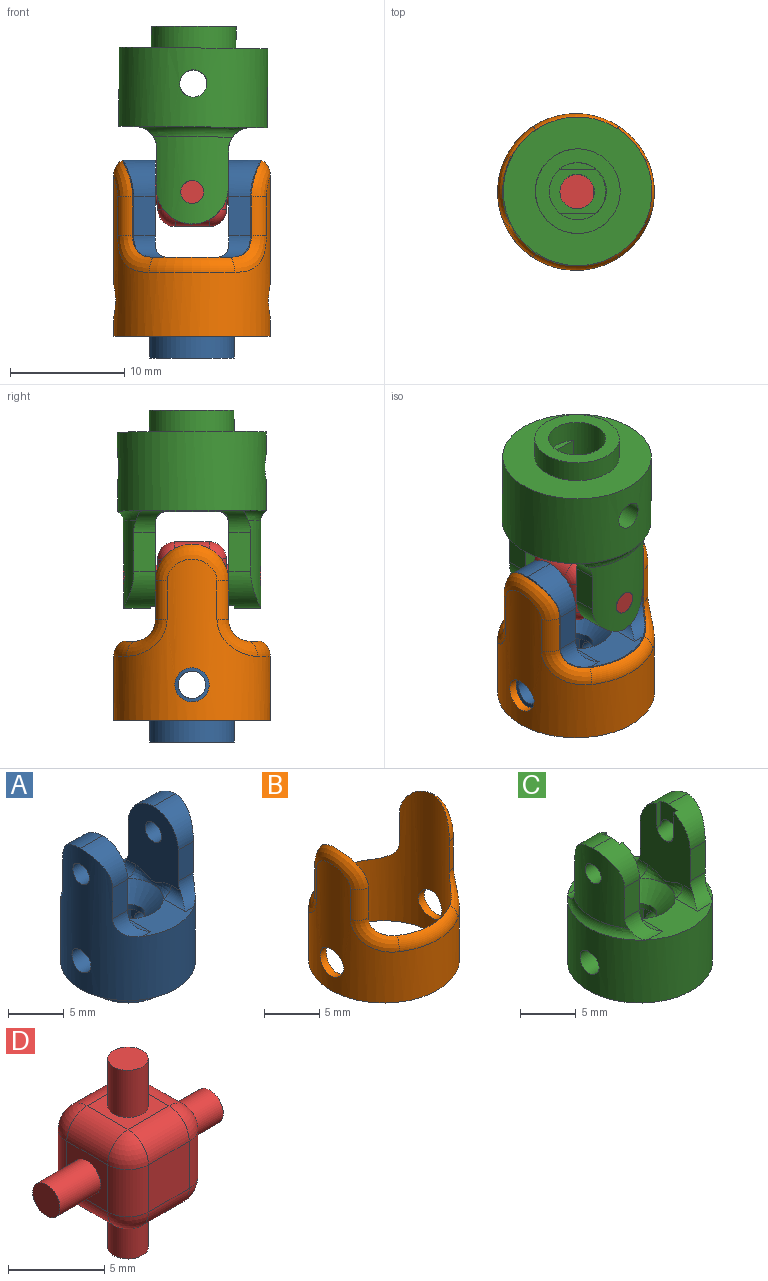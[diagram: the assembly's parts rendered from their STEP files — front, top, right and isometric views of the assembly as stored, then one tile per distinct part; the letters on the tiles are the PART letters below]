
ASSEMBLY  parts=4 mates=3
PART A: 38 faces, bbox 12x12x17.3 mm
  f0: plane 6.48x3.75mm, normal (0,0,1), area 13.8mm2, adj f8,f27,f28,f30,f32,f35
  f1: plane 6.48x3.75mm, normal (0,0,1), area 13.8mm2, adj f8,f27,f29,f31,f34,f37
  f2: cylinder r=2.5mm len=6.6mm, axis (0,0,-1), area 71.9mm2, adj f4,f5,f7,f9,f10,f12
  f3: cylinder r=3.7mm len=7.4mm, axis (0,0,-1), area 44.2mm2, adj f4,f6
  f4: plane 7.4x7.4mm, normal (0,0,-1), area 23.4mm2, adj f2,f3
  f5: plane 3.13x0.55mm, normal (0,0,-1), area 1.2mm2, adj f2,f9
  f6: plane 12x12mm, normal (0,0,-1), area 70.1mm2, adj f3,f8
  f7: plane 4.7x3.13mm, normal (-1,0,0), area 10.2mm2, adj f2,f10,f12,f22
  f8: cylinder r=6mm len=15.4mm, axis (0,0,-1), area 351mm2, adj f0,f1,f6,f13,f14,f16,f18,f19
  f9: plane 4.7x3.13mm, normal (1,0,0), area 10.2mm2, adj f2,f5,f12,f21
  f10: plane 3.13x0.55mm, normal (0,0,-1), area 1.2mm2, adj f2,f7
  f11: cylinder r=1.5mm len=3mm, axis (0,0,-1), area 5.2mm2, adj f12,f27
  f12: plane 5x3.9mm, normal (0,0,-1), area 10.2mm2, adj f2,f7,f9,f11
  f13: plane 3.4x1.91mm, normal (0,1,0), area 6.5mm2, adj f8,f15,f25,f31
  f14: plane 3.4x1.91mm, normal (0,-1,0), area 6.5mm2, adj f8,f15,f26,f30
  f15: plane 8.19x6.75mm, normal (1,0,0), area 40.9mm2, adj f13,f14,f20,f25,f26,f30,f31,f35
  f16: plane 3.4x1.91mm, normal (0,1,0), area 6.5mm2, adj f8,f17,f23,f29
  f17: plane 8.19x6.75mm, normal (-1,0,0), area 40.9mm2, adj f16,f18,f19,f23,f24,f28,f29,f32
  f18: plane 3.4x1.91mm, normal (0,-1,0), area 6.5mm2, adj f8,f17,f24,f28
  f19: cylinder r=1.05mm len=2.8mm, axis (1,0,0), area 18.5mm2, adj f8,f17
  f20: cylinder r=1.05mm len=2.8mm, axis (1,0,0), area 18.5mm2, adj f8,f15
  f21: cylinder r=1.2mm len=4.05mm, axis (1,0,0), area 30.5mm2, adj f8,f9
  f22: cylinder r=1.2mm len=4.05mm, axis (1,0,0), area 30.5mm2, adj f7,f8
  f23: cylinder r=3.2mm len=3.2mm, axis (1,0,0), area 11.7mm2, adj f8,f16,f17,f24
  f24: cylinder r=3.2mm len=3.2mm, axis (-1,0,0), area 11.7mm2, adj f8,f17,f18,f23
  f25: cylinder r=3.2mm len=3.2mm, axis (1,0,0), area 11.7mm2, adj f8,f13,f15,f26
  f26: cylinder r=3.2mm len=3.2mm, axis (-1,0,0), area 11.7mm2, adj f8,f14,f15,f25
  f27: cone r=1.5mm half-angle=45deg, axis (0,0,1), area 34.1mm2, adj f0,f1,f11,f33,f36
  f28: cylinder r=1.9mm len=2.91mm, axis (1,0,0), area 5mm2, adj f0,f8,f17,f18,f32
  f29: cylinder r=1.9mm len=2.91mm, axis (-1,0,0), area 5mm2, adj f1,f8,f16,f17,f34
  f30: cylinder r=1.9mm len=2.91mm, axis (1,0,0), area 5mm2, adj f0,f8,f14,f15,f35
  f31: cylinder r=1.9mm len=2.91mm, axis (-1,0,0), area 5mm2, adj f1,f8,f13,f15,f37
  f32: cylinder r=1mm len=2.8mm, axis (0,-1,0), area 3.1mm2, adj f0,f17,f28,f33
  f33: bspline ~4.87x1.14mm, area 3.8mm2, adj f17,f27,f32,f34
  f34: cylinder r=1mm len=2.8mm, axis (0,-1,0), area 3.1mm2, adj f1,f17,f29,f33
  f35: cylinder r=1mm len=2.8mm, axis (0,1,0), area 3.1mm2, adj f0,f15,f30,f36
  f36: bspline ~4.87x1.14mm, area 3.8mm2, adj f15,f27,f35,f37
  f37: cylinder r=1mm len=2.8mm, axis (0,1,0), area 3.1mm2, adj f1,f15,f31,f36
PART B: 17 faces, bbox 13.7x14.8x15.4 mm
  f0: cylinder r=6.1mm len=15.4mm, axis (0,0,-1), area 358.9mm2, adj f2,f3,f4,f5,f6,f7,f8,f9
  f1: cylinder r=6.85mm len=14.1mm, axis (0,0,-1), area 310mm2, adj f2,f3,f4,f5,f6,f7,f8,f9
  f2: plane 13.7x13.7mm, normal (0,0,-1), area 30.5mm2, adj f0,f1
  f3: cylinder r=1.5mm len=3mm, axis (-1,0,0), area 7.1mm2, adj f0,f1
  f4: cylinder r=1.5mm len=3mm, axis (-1,0,0), area 7.1mm2, adj f0,f1
  f5: bspline ~6.4x3.2mm, area 14.3mm2, adj f0,f1,f6,f7
  f6: cylinder r=1.5mm len=3.4mm, axis (0,0,1), area 5.9mm2, adj f0,f1,f5,f8
  f7: cylinder r=1.5mm len=3.4mm, axis (0,0,1), area 5.9mm2, adj f0,f1,f5,f9
  f8: bspline ~3.54x3.2mm, area 8mm2, adj f0,f1,f6,f10
  f9: bspline ~3.54x3.2mm, area 8mm2, adj f0,f1,f7,f11
  f10: torus R=5.35mm, axis (0,0,1), area 12mm2, adj f0,f1,f8,f12
  f11: torus R=5.35mm, axis (0,0,1), area 12mm2, adj f0,f1,f9,f13
  f12: bspline ~3.54x3.2mm, area 8mm2, adj f0,f1,f10,f14
  f13: bspline ~3.54x3.2mm, area 8mm2, adj f0,f1,f11,f15
  f14: cylinder r=1.5mm len=3.4mm, axis (0,0,1), area 5.9mm2, adj f0,f1,f12,f16
  f15: cylinder r=1.5mm len=3.4mm, axis (0,0,1), area 5.9mm2, adj f0,f1,f13,f16
  f16: bspline ~6.4x3.81mm, area 14.3mm2, adj f0,f1,f14,f15
PART C: 52 faces, bbox 15.2x13x17.3 mm
  f0: plane 8.18x4.25mm, normal (0,0,1), area 17.7mm2, adj f12,f39,f41,f42,f44,f49
  f1: plane 7.99x6.75mm, normal (1,0,0), area 37mm2, adj f4,f17,f19,f25,f26,f28,f29,f37
  f2: plane 7.99x6.75mm, normal (-1,0,0), area 37mm2, adj f3,f21,f22,f30,f31,f33,f34,f35
  f3: cylinder r=1mm len=2.8mm, axis (1,0,0), area 16.2mm2, adj f2,f20,f32,f33,f34
  f4: cylinder r=1mm len=2.8mm, axis (1,0,0), area 16.2mm2, adj f1,f18,f25,f26,f27
  f5: plane 8.18x4.25mm, normal (0,0,1), area 17.7mm2, adj f12,f39,f40,f43,f46,f51
  f6: cylinder r=2.5mm len=6.6mm, axis (0,0,-1), area 71.9mm2, adj f8,f9,f11,f13,f14,f16
  f7: cylinder r=3.7mm len=7.4mm, axis (0,0,-1), area 44.2mm2, adj f8,f10
  f8: plane 7.4x7.4mm, normal (0,0,-1), area 23.4mm2, adj f6,f7
  f9: plane 3.13x0.55mm, normal (0,0,-1), area 1.2mm2, adj f6,f13
  f10: plane 13x13mm, normal (0,0,-1), area 89.7mm2, adj f7,f12
  f11: plane 4.7x3.13mm, normal (-1,0,0), area 10.2mm2, adj f6,f14,f16,f24
  f12: cylinder r=6.5mm len=13mm, axis (0,0,-1), area 272.7mm2, adj f0,f5,f10,f23,f24,f47,f48
  f13: plane 4.7x3.13mm, normal (1,0,0), area 10.2mm2, adj f6,f9,f16,f23
  f14: plane 3.13x0.55mm, normal (0,0,-1), area 1.2mm2, adj f6,f11
  f15: cylinder r=1.5mm len=3mm, axis (0,0,-1), area 5.2mm2, adj f16,f39
  f16: plane 5x3.9mm, normal (0,0,-1), area 10.2mm2, adj f6,f11,f13,f15
  f17: plane 3.4x1.91mm, normal (0,1,0), area 6.5mm2, adj f1,f18,f37,f43
  f18: cylinder r=6mm len=7.63mm, axis (0,0,-1), area 43mm2, adj f4,f17,f19,f37,f38,f42,f43,f48
  f19: plane 3.4x1.91mm, normal (0,-1,0), area 6.5mm2, adj f1,f18,f38,f42
  f20: cylinder r=6mm len=7.63mm, axis (0,0,-1), area 43mm2, adj f3,f21,f22,f35,f36,f40,f41,f47
  f21: plane 3.4x1.91mm, normal (0,1,0), area 6.5mm2, adj f2,f20,f36,f40
  f22: plane 3.4x1.91mm, normal (0,-1,0), area 6.5mm2, adj f2,f20,f35,f41
  f23: cylinder r=1.2mm len=4.55mm, axis (1,0,0), area 33.9mm2, adj f12,f13
  f24: cylinder r=1.2mm len=4.55mm, axis (1,0,0), area 34.3mm2, adj f11,f12
  f25: plane 0.45x0.05mm, normal (0,0,1), area 0mm2, adj f1,f4,f27,f28
  f26: plane 0.45x0.05mm, normal (0,0,1), area 0mm2, adj f1,f4,f27,f29
  f27: plane 2.8x2.1mm, normal (1,0,0), area 4.2mm2, adj f4,f25,f26,f28,f29,f37,f38
  f28: plane 2.61x0.45mm, normal (0,1,0), area 1.2mm2, adj f1,f25,f27,f38
  f29: plane 2.61x0.45mm, normal (0,-1,0), area 1.2mm2, adj f1,f26,f27,f37
  f30: plane 2.61x0.45mm, normal (0,-1,0), area 1.2mm2, adj f2,f32,f34,f36
  f31: plane 2.61x0.45mm, normal (0,1,0), area 1.2mm2, adj f2,f32,f33,f35
  f32: plane 2.8x2.1mm, normal (-1,0,0), area 4.2mm2, adj f3,f30,f31,f33,f34,f35,f36
  f33: plane 0.45x0.05mm, normal (0,0,1), area 0mm2, adj f2,f3,f31,f32
  f34: plane 0.45x0.05mm, normal (0,0,1), area 0mm2, adj f2,f3,f30,f32
  f35: cylinder r=3.2mm len=3.2mm, axis (-1,0,0), area 11.2mm2, adj f2,f20,f22,f31,f32,f36
  f36: cylinder r=3.2mm len=3.2mm, axis (1,0,0), area 11.2mm2, adj f2,f20,f21,f30,f32,f35
  f37: cylinder r=3.2mm len=3.2mm, axis (1,0,0), area 11.2mm2, adj f1,f17,f18,f27,f29,f38
  f38: cylinder r=3.2mm len=3.2mm, axis (-1,0,0), area 11.2mm2, adj f1,f18,f19,f27,f28,f37
  f39: cone r=1.5mm half-angle=45deg, axis (0,0,1), area 34.1mm2, adj f0,f5,f15,f45,f50
  f40: cylinder r=1.9mm len=2.91mm, axis (-1,0,0), area 5.5mm2, adj f2,f5,f20,f21,f46,f47
  f41: cylinder r=1.9mm len=2.91mm, axis (1,0,0), area 5.5mm2, adj f0,f2,f20,f22,f44,f47
  f42: cylinder r=1.9mm len=2.91mm, axis (1,0,0), area 5.5mm2, adj f0,f1,f18,f19,f48,f49
  f43: cylinder r=1.9mm len=2.91mm, axis (-1,0,0), area 5.5mm2, adj f1,f5,f17,f18,f48,f51
  f44: cylinder r=1mm len=2.8mm, axis (0,-1,0), area 3.1mm2, adj f0,f2,f41,f45
  f45: bspline ~4.87x1.14mm, area 3.8mm2, adj f2,f39,f44,f46
  f46: cylinder r=1mm len=2.8mm, axis (0,-1,0), area 3.1mm2, adj f2,f5,f40,f45
  f47: torus R=7mm, axis (0,0,-1), area 9.1mm2, adj f12,f20,f40,f41
  f48: torus R=7mm, axis (0,0,-1), area 9.1mm2, adj f12,f18,f42,f43
  f49: cylinder r=1mm len=2.8mm, axis (0,1,0), area 3.1mm2, adj f0,f1,f42,f50
  f50: bspline ~4.87x1.14mm, area 3.8mm2, adj f1,f39,f49,f51
  f51: cylinder r=1mm len=2.8mm, axis (0,1,0), area 3.1mm2, adj f1,f5,f43,f50
PART D: 34 faces, bbox 12x6x12 mm
  f0: plane 3x3mm, normal (-1,0,0), area 5.9mm2, adj f12,f22,f27,f30,f33
  f1: plane 3x3mm, normal (0,-1,0), area 9mm2, adj f19,f28,f29,f33
  f2: plane 3x3mm, normal (1,0,0), area 5.9mm2, adj f11,f14,f18,f19,f20
  f3: plane 3x3mm, normal (0,1,0), area 9mm2, adj f14,f17,f21,f22
  f4: plane 3x3mm, normal (0,0,1), area 5.5mm2, adj f8,f17,f18,f27,f28
  f5: plane 3x3mm, normal (0,0,-1), area 5.5mm2, adj f7,f20,f21,f29,f30
  f6: plane 2.1x2.1mm, normal (0,0,-1), area 3.5mm2, adj f7
  f7: cylinder r=1.05mm len=3mm, axis (0,0,-1), area 19.8mm2, adj f5,f6
  f8: cylinder r=1.05mm len=3mm, axis (0,0,-1), area 19.8mm2, adj f4,f9
  f9: plane 2.1x2.1mm, normal (0,0,1), area 3.5mm2, adj f8
  f10: plane 2x2mm, normal (1,0,0), area 3.1mm2, adj f11
  f11: cylinder r=1mm len=3mm, axis (-1,0,0), area 18.8mm2, adj f2,f10
  f12: cylinder r=1mm len=3mm, axis (-1,0,0), area 18.8mm2, adj f0,f13
  f13: plane 2x2mm, normal (-1,0,0), area 3.1mm2, adj f12
  f14: cylinder r=1.5mm len=3mm, axis (0,0,1), area 7.1mm2, adj f2,f3,f15,f16
  f15: sphere r=1.5mm, area 3.5mm2, adj f14,f17,f18
  f16: sphere r=1.5mm, area 3.5mm2, adj f14,f20,f21
  f17: cylinder r=1.5mm len=3mm, axis (1,0,0), area 7.1mm2, adj f3,f4,f15,f23
  f18: cylinder r=1.5mm len=3mm, axis (0,-1,0), area 7.1mm2, adj f2,f4,f15,f24
  f19: cylinder r=1.5mm len=3mm, axis (0,0,-1), area 7.1mm2, adj f1,f2,f24,f25
  f20: cylinder r=1.5mm len=3mm, axis (0,1,0), area 7.1mm2, adj f2,f5,f16,f25
  f21: cylinder r=1.5mm len=3mm, axis (-1,0,0), area 7.1mm2, adj f3,f5,f16,f26
  f22: cylinder r=1.5mm len=3mm, axis (0,0,-1), area 7.1mm2, adj f0,f3,f23,f26
  f23: sphere r=1.5mm, area 3.5mm2, adj f17,f22,f27
  f24: sphere r=1.5mm, area 3.5mm2, adj f18,f19,f28
  f25: sphere r=1.5mm, area 3.5mm2, adj f19,f20,f29
  f26: sphere r=1.5mm, area 3.5mm2, adj f21,f22,f30
  f27: cylinder r=1.5mm len=3mm, axis (0,1,0), area 7.1mm2, adj f0,f4,f23,f31
  f28: cylinder r=1.5mm len=3mm, axis (-1,0,0), area 7.1mm2, adj f1,f4,f24,f31
  f29: cylinder r=1.5mm len=3mm, axis (1,0,0), area 7.1mm2, adj f1,f5,f25,f32
  f30: cylinder r=1.5mm len=3mm, axis (0,-1,0), area 7.1mm2, adj f0,f5,f26,f32
  f31: sphere r=1.5mm, area 3.5mm2, adj f27,f28,f33
  f32: sphere r=1.5mm, area 3.5mm2, adj f29,f30,f33
  f33: cylinder r=1.5mm len=3mm, axis (0,0,1), area 7.1mm2, adj f0,f1,f31,f32
PLACE A at identity fixed
PLACE B rot(axis=(0,0,1),0deg) t=(0,0,1.9)mm
PLACE C rot(axis=(0.71,-0.71,0),179.5deg) t=(0.16,0.03,29)mm
PLACE D rot(axis=(0.58,0.58,0.58),119.9deg) t=(-2.98,-3.01,11.51)mm
MATE revolute A.f19 <-> D.f7  axis (1,0,0) through (6.02,0,14.5)mm
MATE revolute B.f0 <-> A.f8  axis (0,0,-1) through (0,0,1.9)mm
MATE revolute C.f3 <-> D.f11  axis (0,-1,0) through (0.02,6,14.48)mm
